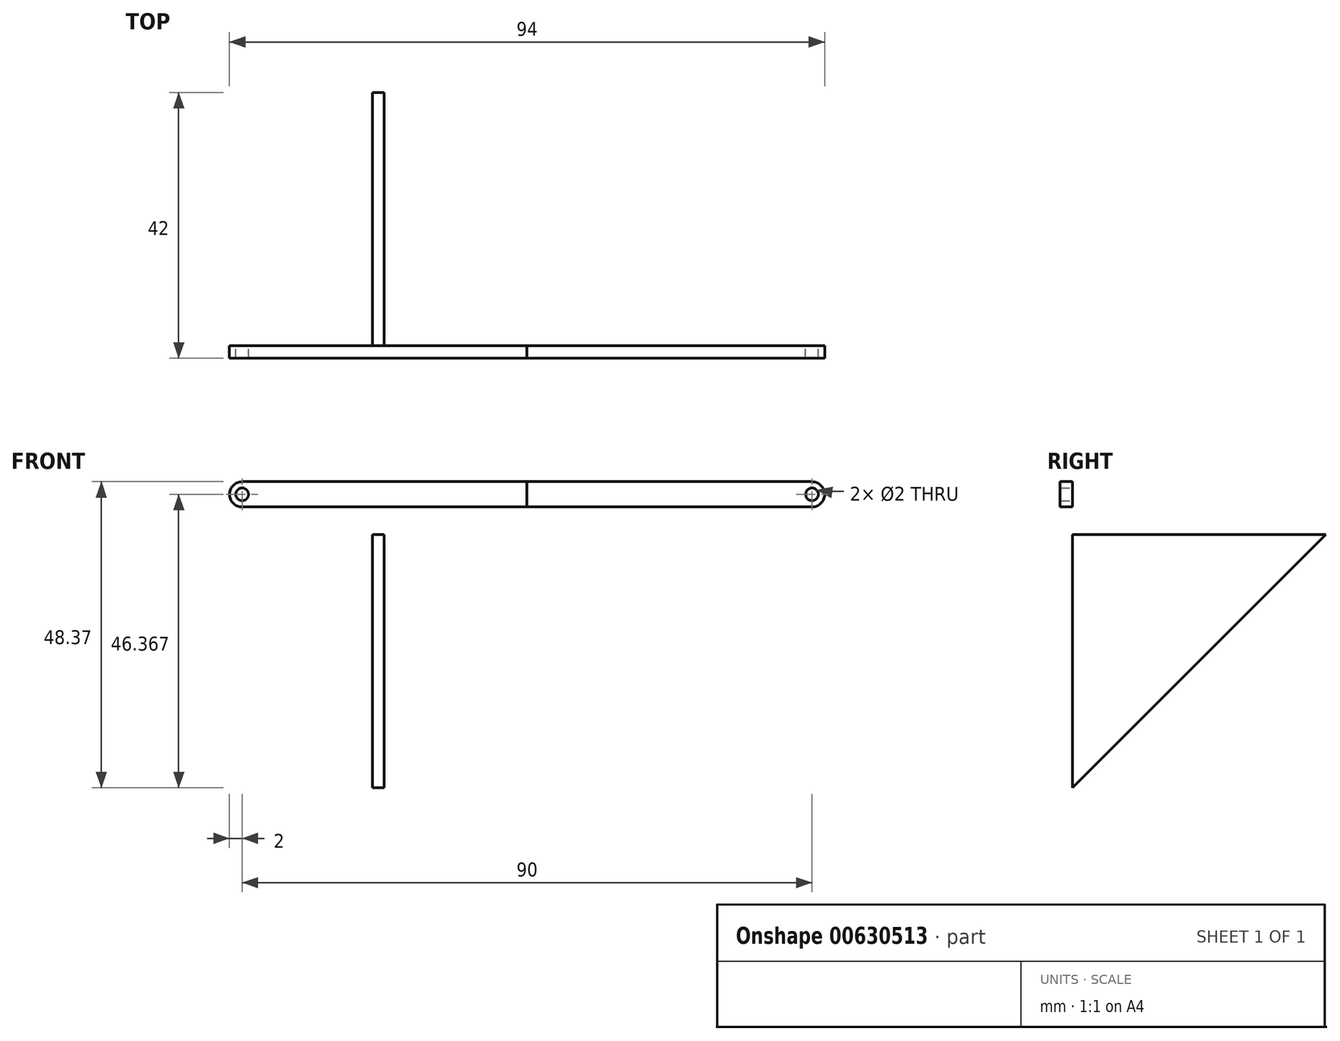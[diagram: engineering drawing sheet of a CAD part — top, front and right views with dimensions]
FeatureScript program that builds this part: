
annotation { "Feature Type Name" : "Feature", "Feature Type Description" : "" }
export const myFeature = defineFeature(function(context is Context, id is Id, definition is map)
    precondition{}
    {
        {
            var Q0;
            Q0=qCreatedBy(makeId("Right.planeOp"),FACE);
            var sketch = newSketch(context, id + "F0", { "sketchPlane" : qUnion([Q0])});
            skLineSegment(sketch, "E0", {"start": v(0, 0) * mm, "end": v(40, 0) * mm});
            skLineSegment(sketch, "E1", {"start": v(40, 0) * mm, "end": v(0, -40) * mm});
            skLineSegment(sketch, "E2", {"start": v(0, -40) * mm, "end": v(0, 0) * mm});
            skSolve(sketch);
        }
        {
            var Q0;
            Q0 = qSketchRegion(id + "F0", true);
            extrude(context, id + "F1", {"entities" : qUnion([Q0]), "endBound" : BoundingType.SYMMETRIC, "depth" : 1.8 * mm, "offsetDistance" : 25 * mm});
        }
        {
            var Q0;
            Q0=qCreatedBy(makeId("Front.planeOp"),FACE);
            var sketch = newSketch(context, id + "F2", { "sketchPlane" : qUnion([Q0])});
            skLineSegment(sketch, "E3.bottom", {"start": v(23.5, 8.37) * mm, "end": v(-21.5, 8.37) * mm});
            skLineSegment(sketch, "E3.top", {"start": v(23.5, 4.37) * mm, "end": v(-21.5, 4.37) * mm});
            skLineSegment(sketch, "E3.left", {"start": v(23.5, 8.37) * mm, "end": v(23.5, 4.37) * mm});
            skLineSegment(sketch, "E3.right", {"start": v(-23.5, 6.37) * mm, "end": v(-23.5, 6.37) * mm});
            skPoint(sketch, "E3.middle", {"position": v(0, 6.37) * mm});
            skPoint(sketch, "E4.visualSharp", {"position": v(-23.5, 8.37) * mm});
            skArc(sketch, "E4.filletArc", {"start": v(-21.5, 8.37) * mm, "mid": v(-22.91, 7.78) * mm, "end": v(-23.5, 6.37) * mm});
            skPoint(sketch, "E5.visualSharp", {"position": v(-23.5, 4.37) * mm});
            skArc(sketch, "E5.filletArc", {"start": v(-23.5, 6.37) * mm, "mid": v(-22.91, 4.95) * mm, "end": v(-21.5, 4.37) * mm});
            skCircle(sketch, "E6", {"center": v(-21.5, 6.37) * mm, "radius": 1 * mm});
            skSolve(sketch);
        }
        {
            var Q0;
            Q0 = qSketchRegion(id + "F2", true);
            extrude(context, id + "F3", {"entities" : qUnion([Q0]), "depth" : 2 * mm, "offsetDistance" : 25 * mm});
        }
        {
            var Q0;
            Q0=makeQuery(id+"F3.opExtrude","SWEPT_BODY",BODY,{"disambiguationData":[OSD([sQuery(id+"F2.wireOp",EDGE,"E3.bottom"),sQuery(id+"F2.wireOp",EDGE,"E3.top"),sQuery(id+"F2.wireOp",EDGE,"E3.left"),sQuery(id+"F2.wireOp",EDGE,"E4.filletArc"),sQuery(id+"F2.wireOp",EDGE,"E5.filletArc"),sQuery(id+"F2.wireOp",EDGE,"E6")])]});
            var Q1;
            Q1=makeQuery(id+"F3.opExtrude","SWEPT_FACE",FACE,{"disambiguationData":[OSD([sQuery(id+"F2.wireOp",EDGE,"E3.left")])]});
            mirror(context, id + "F4", {"operationType" : NewBodyOperationType.ADD, "entities" : qUnion([Q0]), "mirrorPlane" : qUnion([Q1])});
        }
    });
